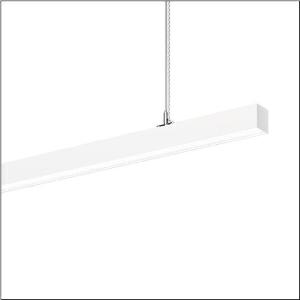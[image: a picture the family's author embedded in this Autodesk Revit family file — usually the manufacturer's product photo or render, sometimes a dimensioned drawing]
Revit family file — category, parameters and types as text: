
# Revit family: silica_r__21_51mx30tct9w_581c
name_source: partatom
category: Lighting Fixtures
units: mm (PartAtom-declared; Revit-internal decimal feet)

## family parameters
Cut with Voids When Loaded = No
Host = Face
Light Source = No
Part Type = Normal
Room Calculation Point = No
Round Connector Dimension = Use Diameter
Shared = No

## types (1)
- --- (1 x LED, 10300 lm, 84.4 W, 6500K)
    Apparent Load = 84 VA
    CIE Flux Codes = 47 79 96 58 100
    Color Rendering = 80
    Color Temperature = 6500K
    Default Elevation = 1800 mm
    Description = Silica® 21, office luminaire, primary optical cover: cover, of PMMA, opal, light emission: direct/indirect distribution, primary light characteristic: symmetric, installation type: suspended mounting, LED, rated luminous flux: 10.300lm, luminous efficacy: 116lm/W, light colour: 8tw, colour temperature: 2700..6500K, control gear: ECG DALI, with terminal, 3+2-pole, max. 2.5mm², mains connection: 220..240V, AC, 50/60Hz, rated input power: 88.7W, luminaire housing, of aluminium, traffic white (RAL 9016), length: 3.004mm, width: 53mm, height: 53mm, protection rating (complete): IP20, insulation class (complete): insulation class I (protective earthing), certification: CE, permissible operating ambient temperature: 0..+35°C, standard: EN 50419, packaging unit: 1 piece
    Height = 53 mm
    Lamp = 1 x LED
    Lamp Light Flux = 10300 lm
    Lamp Power = 84.4 W
    Lamp count = 1
    Length = 3004 mm
    Luminous efficacy = 122 lm/W
    Manufacturer = Siteco
    ModVariant = No
    Model = 51MX30TCT9W
    Mounting Place = Ceiling
    Mounting Type = Pendant
    Number of Poles = 1
    OnlyDefault = Yes
    Power Factor = 1
    Product Name = Silica® 21
    Product group = office luminaire | ceiling pendant
    ProductGroupID = 902
    Protection Class = Protection class I
    Protection Degree = IP 20
    RLX_Detail_Level = 1
    RLX_Emergency_Light_Flux = 0 lm
    RLX_Emergency_Type = 0
    RLX_Emergency_Type_DB = No
    RlxData = <blob elided: 18105 chars, md5=3218a713>
    Socket = socket
    Standby Power = 0 W
    System Light Flux = 10300 lm
    System Power = 84 W
    Type Comments = individual setting
    Type Image = l_1335916.jpg
    URL = http://relux.com
    VarID = @adj_109447
    Voltage = 0 V
    Weight = 0.00 kg
    Width = 53 mm

## geometry (parser evidence)
native form markers: Blend x4, Sweep x13
no freeform markers — native parametric forms only
